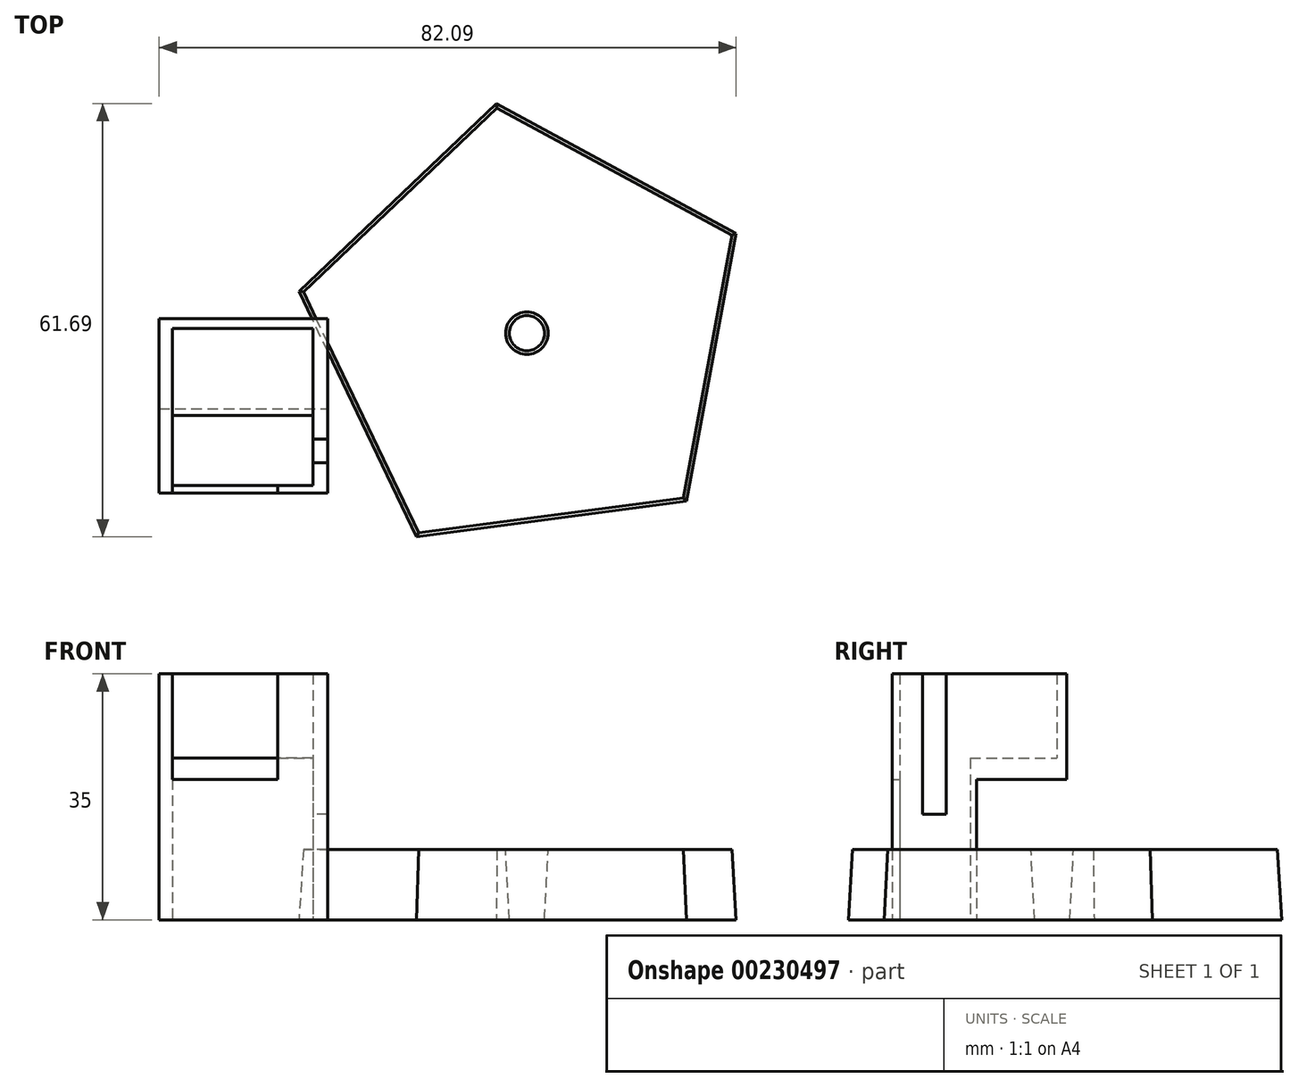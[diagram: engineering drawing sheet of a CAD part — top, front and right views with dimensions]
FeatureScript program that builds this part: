
annotation { "Feature Type Name" : "Feature", "Feature Type Description" : "" }
export const myFeature = defineFeature(function(context is Context, id is Id, definition is map)
    precondition{}
    {
        {
            var Q0;
            Q0=qCreatedBy(makeId("Top.planeOp"),FACE);
            var sketch = newSketch(context, id + "F0", { "sketchPlane" : qUnion([Q0])});
            skLineSegment(sketch, "E0.bottom", {"start": v(-50.44, -11.68) * mm, "end": v(-30.44, -11.68) * mm});
            skLineSegment(sketch, "E0.top", {"start": v(-50.44, -21.68) * mm, "end": v(-30.44, -21.68) * mm});
            skLineSegment(sketch, "E0.left", {"start": v(-50.44, -11.68) * mm, "end": v(-50.44, -21.68) * mm});
            skLineSegment(sketch, "E0.right", {"start": v(-30.44, -11.68) * mm, "end": v(-30.44, -21.68) * mm});
            skLineSegment(sketch, "E1.bottom", {"start": v(-52.34, -22.77) * mm, "end": v(-28.34, -22.77) * mm});
            skLineSegment(sketch, "E1.top", {"start": v(-52.34, -10.77) * mm, "end": v(-28.34, -10.77) * mm});
            skLineSegment(sketch, "E1.left", {"start": v(-52.34, -22.77) * mm, "end": v(-52.34, -10.77) * mm});
            skLineSegment(sketch, "E1.right", {"start": v(-28.34, -22.77) * mm, "end": v(-28.34, -10.77) * mm});
            skSolve(sketch);
        }
        {
            var Q0;
            Q0=makeQuery(id+"F0.imprint","IMPRINT",FACE,{"disambiguationData":[TD([[makeQuery(id+"F0.imprint","IMPRINT",EDGE,{"derivedFrom":sQuery(id+"F0.wireOp",EDGE,"E0.bottom")}),1.0]])]});
            extrude(context, id + "F1", {"entities" : qUnion([Q0]), "depth" : 15 * mm});
        }
        {
            var Q0;
            Q0=makeQuery(id+"F1.opExtrude","CAP_FACE",FACE,{"disambiguationData":[OSD([sQuery(id+"F0.wireOp",EDGE,"E0.bottom"),sQuery(id+"F0.wireOp",EDGE,"E0.top"),sQuery(id+"F0.wireOp",EDGE,"E0.left"),sQuery(id+"F0.wireOp",EDGE,"E0.right"),sQuery(id+"F0.wireOp",EDGE,"E1.bottom"),sQuery(id+"F0.wireOp",EDGE,"E1.top"),sQuery(id+"F0.wireOp",EDGE,"E1.left"),sQuery(id+"F0.wireOp",EDGE,"E1.right")])],"isStart":false});
            var sketch = newSketch(context, id + "F2", { "sketchPlane" : qUnion([Q0])});
            skLineSegment(sketch, "E2", {"start": v(-30.44, -21.68) * mm, "end": v(-30.44, -18.45) * mm});
            skLineSegment(sketch, "E3", {"start": v(-28.34, -10.77) * mm, "end": v(-28.34, -15.08) * mm});
            skLineSegment(sketch, "E4", {"start": v(-28.34, -22.77) * mm, "end": v(-28.34, -18.45) * mm});
            skLineSegment(sketch, "E5", {"start": v(-28.34, -15.08) * mm, "end": v(-30.44, -15.08) * mm});
            skLineSegment(sketch, "E6", {"start": v(-28.34, -18.45) * mm, "end": v(-30.44, -18.45) * mm});
            skLineSegment(sketch, "E7.trimOffspring", {"start": v(-30.44, -15.08) * mm, "end": v(-30.44, -11.68) * mm});
            skLineSegment(sketch, "E8", {"start": v(-30.44, -11.68) * mm, "end": v(-50.44, -11.68) * mm});
            skLineSegment(sketch, "E9", {"start": v(-50.44, -11.68) * mm, "end": v(-50.44, -21.68) * mm});
            skLineSegment(sketch, "E10", {"start": v(-50.44, -21.68) * mm, "end": v(-30.44, -21.68) * mm});
            skLineSegment(sketch, "E11", {"start": v(-52.34, -10.77) * mm, "end": v(-52.34, -22.77) * mm});
            skLineSegment(sketch, "E12", {"start": v(-52.34, -22.77) * mm, "end": v(-28.34, -22.77) * mm});
            skLineSegment(sketch, "E13", {"start": v(-52.34, -10.77) * mm, "end": v(-28.34, -10.77) * mm});
            skSolve(sketch);
        }
        {
            var Q0;
            Q0=makeQuery(id+"F2.imprint","IMPRINT",FACE,{"disambiguationData":[TD([[makeQuery(id+"F2.imprint","IMPRINT",EDGE,{"derivedFrom":sQuery(id+"F2.wireOp",EDGE,"E2")}),1.0]])]});
            extrude(context, id + "F3", {"entities" : qUnion([Q0]), "operationType" : NewBodyOperationType.ADD, "depth" : 5 * mm});
        }
        {
            var Q0;
            Q0=makeQuery(id+"F3.opExtrude","CAP_FACE",FACE,{"disambiguationData":[OSD([sQuery(id+"F2.wireOp",EDGE,"E2"),sQuery(id+"F2.wireOp",EDGE,"E3"),sQuery(id+"F2.wireOp",EDGE,"E4"),sQuery(id+"F2.wireOp",EDGE,"E5"),sQuery(id+"F2.wireOp",EDGE,"E6"),sQuery(id+"F2.wireOp",EDGE,"E7.trimOffspring"),sQuery(id+"F2.wireOp",EDGE,"E8"),sQuery(id+"F2.wireOp",EDGE,"E9"),sQuery(id+"F2.wireOp",EDGE,"E10"),sQuery(id+"F2.wireOp",EDGE,"E11"),sQuery(id+"F2.wireOp",EDGE,"E12"),sQuery(id+"F2.wireOp",EDGE,"E13")])],"isStart":false});
            var sketch = newSketch(context, id + "F4", { "sketchPlane" : qUnion([Q0])});
            skPoint(sketch, "E14.left.end.orphan", {"position": v(-52.34, -5.77) * mm});
            skPoint(sketch, "E14.right.end.orphan", {"position": v(-28.34, -5.77) * mm});
            skLineSegment(sketch, "E15.top", {"start": v(-50.44, 0.67) * mm, "end": v(-30.44, 0.67) * mm});
            skLineSegment(sketch, "E15.left", {"start": v(-50.44, -9.33) * mm, "end": v(-50.44, 0.67) * mm});
            skLineSegment(sketch, "E15.right", {"start": v(-30.44, -9.33) * mm, "end": v(-30.44, 0.67) * mm});
            skLineSegment(sketch, "E16", {"start": v(-52.34, -10.77) * mm, "end": v(-52.34, 2.04) * mm});
            skLineSegment(sketch, "E17", {"start": v(-28.34, -10.77) * mm, "end": v(-28.34, 2.04) * mm});
            skLineSegment(sketch, "E18", {"start": v(-28.34, 2.04) * mm, "end": v(-52.34, 2.04) * mm});
            skLineSegment(sketch, "E19", {"start": v(-50.44, -9.33) * mm, "end": v(-50.44, -10.77) * mm});
            skLineSegment(sketch, "E20", {"start": v(-30.44, -9.33) * mm, "end": v(-30.44, -10.77) * mm});
            skLineSegment(sketch, "E21", {"start": v(-52.34, -10.77) * mm, "end": v(-52.34, -22.77) * mm});
            skLineSegment(sketch, "E22", {"start": v(-28.34, -22.77) * mm, "end": v(-28.34, -18.45) * mm});
            skLineSegment(sketch, "E23", {"start": v(-28.34, -18.45) * mm, "end": v(-30.44, -18.45) * mm});
            skLineSegment(sketch, "E24", {"start": v(-30.44, -18.45) * mm, "end": v(-30.44, -21.68) * mm});
            skLineSegment(sketch, "E25", {"start": v(-50.44, -21.68) * mm, "end": v(-50.44, -11.68) * mm});
            skLineSegment(sketch, "E26", {"start": v(-30.44, -11.68) * mm, "end": v(-30.44, -15.08) * mm});
            skLineSegment(sketch, "E27", {"start": v(-30.44, -15.08) * mm, "end": v(-28.34, -15.08) * mm});
            skLineSegment(sketch, "E28", {"start": v(-28.34, -15.08) * mm, "end": v(-28.34, -10.77) * mm});
            skLineSegment(sketch, "E29", {"start": v(-50.44, -10.77) * mm, "end": v(-50.44, -11.68) * mm});
            skLineSegment(sketch, "E30", {"start": v(-30.44, -10.77) * mm, "end": v(-30.44, -11.68) * mm});
            skPoint(sketch, "E31", {"position": v(-35.44, -22.77) * mm});
            skPoint(sketch, "E32", {"position": v(-51.21, -22.77) * mm});
            skLineSegment(sketch, "E33", {"start": v(-50.44, -21.68) * mm, "end": v(-50.44, -22.77) * mm});
            skPoint(sketch, "E34", {"position": v(-50.44, -22.77) * mm});
            skLineSegment(sketch, "E35", {"start": v(-35.44, -22.77) * mm, "end": v(-35.44, -21.68) * mm});
            skLineSegment(sketch, "E36", {"start": v(-52.34, -22.77) * mm, "end": v(-50.44, -22.77) * mm});
            skLineSegment(sketch, "E37.bottom", {"start": v(-35.44, -21.68) * mm, "end": v(-30.44, -21.68) * mm});
            skLineSegment(sketch, "E37.top", {"start": v(-35.44, -22.77) * mm, "end": v(-28.34, -22.77) * mm});
            skLineSegment(sketch, "E37.left", {"start": v(-35.44, -21.68) * mm, "end": v(-35.44, -22.77) * mm});
            skLineSegment(sketch, "E37.right", {"start": v(-28.34, -21.68) * mm, "end": v(-28.34, -22.77) * mm});
            skSolve(sketch);
        }
        {
            var Q0;
            Q0=makeQuery(id+"F4.imprint","IMPRINT",FACE,{"disambiguationData":[TD([[makeQuery(id+"F4.imprint","IMPRINT",EDGE,{"derivedFrom":sQuery(id+"F4.wireOp",EDGE,"E15.top")}),-1.0]])]});
            var Q1;
            {var subQ0=sQuery(id+"F4.wireOp",EDGE,"E29");Q1=makeQuery(id+"F4.imprint","IMPRINT",FACE,{"disambiguationData":[TD([[makeQuery(id+"F4.imprint","IMPRINT",EDGE,{"derivedFrom":subQ0}),1.0]])]});}
            var Q2;
            {var subQ0=sQuery(id+"F4.wireOp",EDGE,"E21");Q2=makeQuery(id+"F4.imprint","IMPRINT",FACE,{"disambiguationData":[TD([[makeQuery(id+"F4.imprint","IMPRINT",EDGE,{"derivedFrom":subQ0}),-1.0]])]});}
            var Q3;
            Q3=makeQuery(id+"F4.imprint","IMPRINT",FACE,{"disambiguationData":[TD([[makeQuery(id+"F4.imprint","IMPRINT",EDGE,{"derivedFrom":sQuery(id+"F4.wireOp",EDGE,"E15.top")}),1.0]])]});
            var Q4;
            Q4=makeQuery(id+"F4.imprint","IMPRINT",FACE,{"disambiguationData":[TD([[makeQuery(id+"F4.imprint","IMPRINT",EDGE,{"derivedFrom":sQuery(id+"F4.wireOp",EDGE,"E26")}),1.0]])]});
            extrude(context, id + "F5", {"entities" : qUnion([Q0, Q1, Q2, Q3, Q4]), "operationType" : NewBodyOperationType.ADD, "depth" : 3 * mm});
        }
        {
            var Q0;
            Q0 = qSketchRegion(id + "F4", true);
            extrude(context, id + "F6", {"entities" : qUnion([Q0]), "operationType" : NewBodyOperationType.ADD, "depth" : 15 * mm});
        }
        {
            var Q0;
            Q0=qCreatedBy(makeId("Top.planeOp"),FACE);
            var sketch = newSketch(context, id + "F7", { "sketchPlane" : qUnion([Q0])});
            skCircle(sketch, "E38.cCircle", {"center": v(0, 0) * mm, "radius": 26.68 * mm, "construction": true});
            skLineSegment(sketch, "E38.0", {"start": v(22.73, -23.9) * mm, "end": v(-15.7, -29) * mm});
            skLineSegment(sketch, "E38.1", {"start": v(-15.7, -29) * mm, "end": v(-32.43, 5.97) * mm});
            skLineSegment(sketch, "E38.2", {"start": v(-32.43, 5.97) * mm, "end": v(-4.34, 32.7) * mm});
            skLineSegment(sketch, "E38.3", {"start": v(-4.34, 32.7) * mm, "end": v(29.75, 14.23) * mm});
            skLineSegment(sketch, "E38.4", {"start": v(29.75, 14.23) * mm, "end": v(22.73, -23.9) * mm});
            skPoint(sketch, "E38.0.midPoint", {"position": v(3.51, -26.45) * mm});
            skCircle(sketch, "E39", {"center": v(0, 0) * mm, "radius": 2.5 * mm});
            skLineSegment(sketch, "E40", {"start": v(0, 2.5) * mm, "end": v(0, -2.5) * mm});
            skSolve(sketch);
        }
        {
            var Q0;
            Q0=makeQuery(id+"F7.imprint","IMPRINT",FACE,{"disambiguationData":[TD([[makeQuery(id+"F7.imprint","IMPRINT",EDGE,{"derivedFrom":sQuery(id+"F7.wireOp",EDGE,"E38.0")}),-1.0]])]});
            extrude(context, id + "F8", {"entities" : qUnion([Q0]), "depth" : 10 * mm, "hasDraft" : true, "draftAngle" : 3 * degree, "draftPullDirection" : true});
        }
    });
